# Revit family: Sanitary_Taps-Mixers_hansgrohe_72449XXX-Rebris-S-Single-lever-bath-mixe_NEW
name_source: partatom
category: Plumbing Fixtures
revit_build: Autodesk Revit 2018 (Build: 20170223_1515(x64)
units: mm (PartAtom-declared; Revit-internal decimal feet)

## family parameters
Always vertical = No
Cut with Voids When Loaded = No
OmniClass Number = 23.45.55.17
OmniClass Title = Mixing Faucets
Part Type = Normal
Room Calculation Point = No
Round Connector Dimension = Use Diameter
Shared = No
Work Plane-Based = Yes

## types (2) — shared parameters
Always visible = Yes
BIMobject category = Taps & Mixers
Default Elevation = 1219.2 mm  [stored 4 ft]
Description = Rebris S Single lever bath mixer for concealed installation
Design country = Germany
EAN code = 4059625412848
Edition number = 1
GTIN code = https://4059625412848
IFC Classification = Valve
Manufacturer = Hansgrohe
Manufacturer country = Germany
Manufacturer name = hansgrohe
Model = 72449XXX
OmniClass Code = 23-31 11 00
OmniClass Description = Faucets
Product Guid = 0a216440-5428-4160-921d-42106e1fd107
Product SKU = 72449XXX
Product data url = https://bimobject.com
Product family = Rebris S
Product group = Bath mixers
Product name = 72449XXX Rebris S Single lever bath mixer for concealed installation
QR code = https://bimobject.com
UNSPSC Code = 301815
URL = https://www.hansgrohe.com
Weight Net (Kg) = 2

## per-type parameters (varying)
| type | Material 1 |
| 670 Matte Black | Hansgrohe - Metal - 670 Matte Black |
| 000 Chrome | Hansgrohe - Metal - 000 Chrome |

note: [stored X ft] marks values corroborated as IEEE doubles in the binary element streams (Revit-internal decimal feet)

## geometry (parser evidence)
native form markers: Sweep x2
no freeform markers — native parametric forms only
